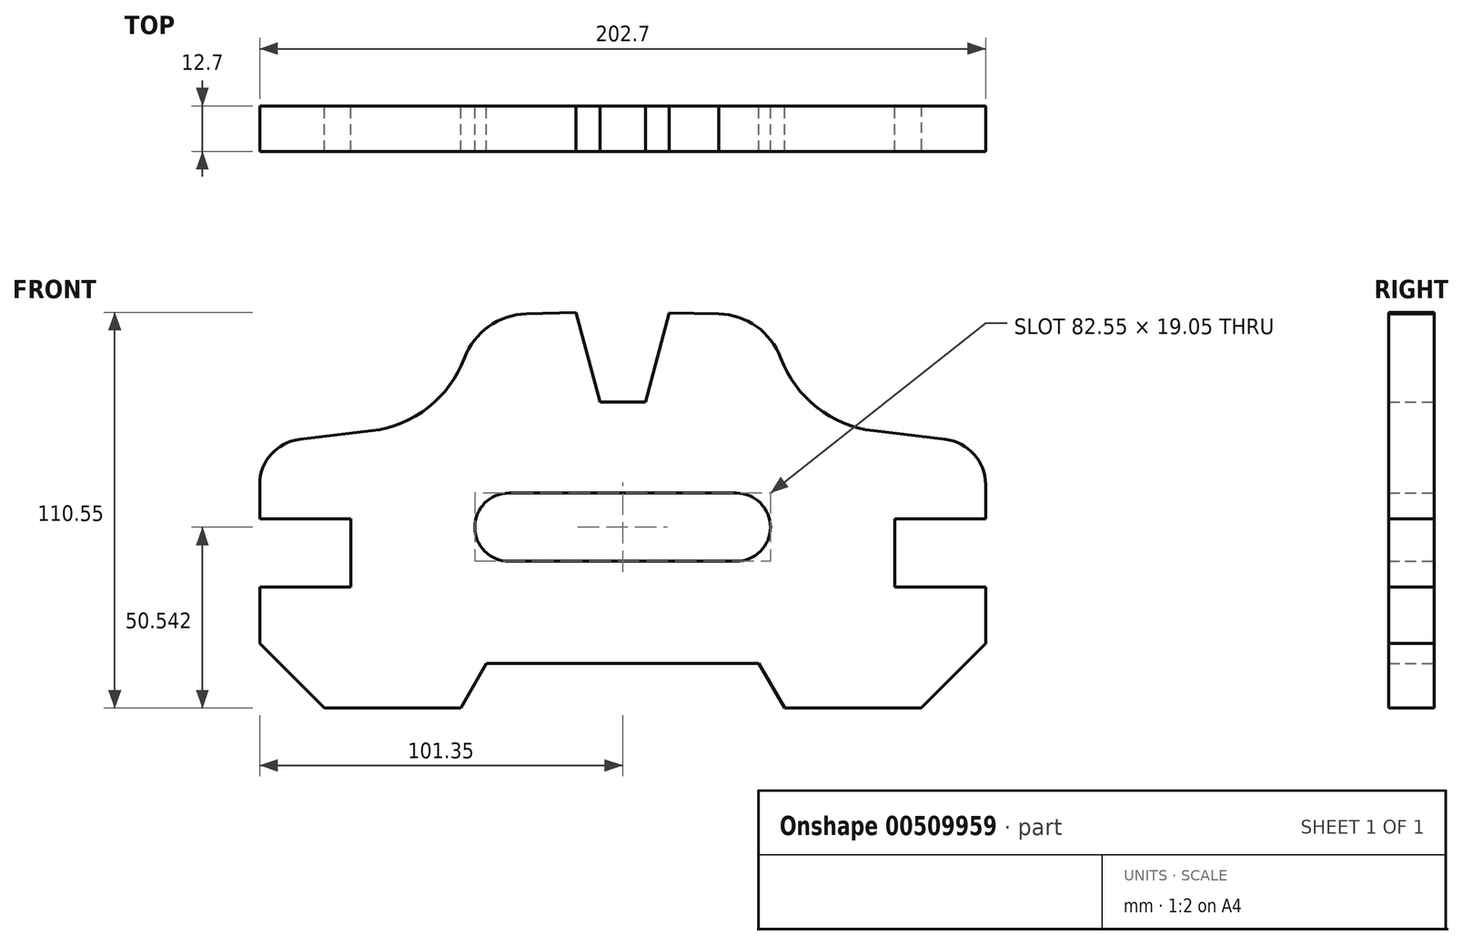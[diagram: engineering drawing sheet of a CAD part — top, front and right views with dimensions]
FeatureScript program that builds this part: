
annotation { "Feature Type Name" : "Feature", "Feature Type Description" : "" }
export const myFeature = defineFeature(function(context is Context, id is Id, definition is map)
    precondition{}
    {
        {
            var Q0;
            Q0=qCreatedBy(makeId("Front.planeOp"),FACE);
            var sketch = newSketch(context, id + "F0", { "sketchPlane" : qUnion([Q0])});
            skLineSegment(sketch, "E0", {"start": v(0, 64.43) * mm, "end": v(0, -63.1) * mm, "construction": true});
            skLineSegment(sketch, "E1", {"start": v(38.03, -38.44) * mm, "end": v(45.21, -50.88) * mm});
            skLineSegment(sketch, "E2", {"start": v(45.21, -50.88) * mm, "end": v(101.35, -50.88) * mm});
            skLineSegment(sketch, "E3", {"start": v(101.35, -50.88) * mm, "end": v(101.35, -17.1) * mm});
            skLineSegment(sketch, "E4", {"start": v(101.35, -17.1) * mm, "end": v(75.95, -17.1) * mm});
            skLineSegment(sketch, "E5", {"start": v(75.95, -17.1) * mm, "end": v(75.95, 1.95) * mm});
            skLineSegment(sketch, "E6", {"start": v(75.95, 1.95) * mm, "end": v(101.35, 1.95) * mm});
            skLineSegment(sketch, "E7", {"start": v(101.35, 1.95) * mm, "end": v(101.35, 11.6) * mm});
            skLineSegment(sketch, "E8", {"start": v(38.03, -38.44) * mm, "end": v(0, -38.44) * mm});
            skLineSegment(sketch, "E9", {"start": v(0, 9.19) * mm, "end": v(31.75, 9.19) * mm});
            skLineSegment(sketch, "E10", {"start": v(0, -9.86) * mm, "end": v(31.75, -9.86) * mm});
            skLineSegment(sketch, "E11.MirrorCS", {"start": v(-101.35, 1.95) * mm, "end": v(-101.35, 11.6) * mm});
            skLineSegment(sketch, "E12.MirrorCS", {"start": v(-75.95, 1.95) * mm, "end": v(-101.35, 1.95) * mm});
            skLineSegment(sketch, "E13.MirrorCS", {"start": v(-75.95, -17.1) * mm, "end": v(-75.95, 1.95) * mm});
            skLineSegment(sketch, "E14.MirrorCS", {"start": v(-101.35, -17.1) * mm, "end": v(-75.95, -17.1) * mm});
            skLineSegment(sketch, "E15.MirrorCS", {"start": v(-101.35, -50.88) * mm, "end": v(-101.35, -17.1) * mm});
            skLineSegment(sketch, "E16.MirrorCS", {"start": v(-45.21, -50.88) * mm, "end": v(-101.35, -50.88) * mm});
            skLineSegment(sketch, "E17.MirrorCS", {"start": v(-38.03, -38.44) * mm, "end": v(-45.21, -50.88) * mm});
            skLineSegment(sketch, "E18.MirrorCS", {"start": v(-38.03, -38.44) * mm, "end": v(0, -38.44) * mm});
            skLineSegment(sketch, "E19.MirrorCS", {"start": v(0, -9.86) * mm, "end": v(-31.75, -9.86) * mm});
            skLineSegment(sketch, "E20.MirrorCS", {"start": v(0, 9.19) * mm, "end": v(-31.75, 9.19) * mm});
            skArc(sketch, "E21", {"start": v(-31.75, 9.19) * mm, "mid": v(-41.27, -0.34) * mm, "end": v(-31.75, -9.86) * mm});
            skArc(sketch, "E22", {"start": v(31.75, -9.86) * mm, "mid": v(41.27, -0.34) * mm, "end": v(31.75, 9.19) * mm});
            skLineSegment(sketch, "E23", {"start": v(0, 34.64) * mm, "end": v(6.35, 34.64) * mm});
            skLineSegment(sketch, "E24.MirrorCS", {"start": v(0, 34.64) * mm, "end": v(-6.35, 34.64) * mm});
            skLineSegment(sketch, "E25", {"start": v(6.35, 34.64) * mm, "end": v(6.35, 73.1) * mm, "construction": true});
            skLineSegment(sketch, "E26", {"start": v(-6.35, 34.64) * mm, "end": v(-6.35, 69.53) * mm, "construction": true});
            skLineSegment(sketch, "E27", {"start": v(38.03, -38.44) * mm, "end": v(38.03, -60.96) * mm, "construction": true});
            skLineSegment(sketch, "E28.MirrorCS", {"start": v(13.01, 59.51) * mm, "end": v(6.35, 34.64) * mm});
            skLineSegment(sketch, "E29.MirrorCS", {"start": v(-13.06, 59.67) * mm, "end": v(-6.35, 34.64) * mm});
            skLineSegment(sketch, "E30", {"start": v(-26.86, 59.28) * mm, "end": v(-13.06, 59.67) * mm});
            skLineSegment(sketch, "E31", {"start": v(13.01, 59.51) * mm, "end": v(26.86, 59.28) * mm});
            skArc(sketch, "E32", {"start": v(-101.35, 11.6) * mm, "mid": v(-98.14, 20.03) * mm, "end": v(-90.15, 24.21) * mm});
            skLineSegment(sketch, "E33", {"start": v(-90.15, 24.21) * mm, "end": v(-70.1, 26.6) * mm});
            skArc(sketch, "E34", {"start": v(-70.1, 26.6) * mm, "mid": v(-54.28, 33.14) * mm, "end": v(-44.15, 46.95) * mm});
            skArc(sketch, "E35", {"start": v(-44.15, 46.95) * mm, "mid": v(-37.38, 55.75) * mm, "end": v(-26.86, 59.28) * mm});
            skArc(sketch, "E36.MirrorCS", {"start": v(101.35, 11.6) * mm, "mid": v(98.14, 20.03) * mm, "end": v(90.15, 24.21) * mm});
            skLineSegment(sketch, "E37.MirrorCS", {"start": v(90.15, 24.21) * mm, "end": v(70.1, 26.6) * mm});
            skArc(sketch, "E38.MirrorCS", {"start": v(70.1, 26.6) * mm, "mid": v(54.28, 33.14) * mm, "end": v(44.15, 46.95) * mm});
            skArc(sketch, "E39.MirrorCS", {"start": v(44.15, 46.95) * mm, "mid": v(37.38, 55.75) * mm, "end": v(26.86, 59.28) * mm});
            skSolve(sketch);
        }
        {
            var Q0;
            Q0=makeQuery(id+"F0.imprint","IMPRINT",FACE,{"disambiguationData":[TD([[makeQuery(id+"F0.imprint","IMPRINT",EDGE,{"derivedFrom":sQuery(id+"F0.wireOp",EDGE,"E1")}),1.0]])]});
            extrude(context, id + "F1", {"entities" : qUnion([Q0]), "depth" : 12.7 * mm});
        }
        {
            var Q0;
            Q0=makeQuery(id+"F1.opExtrude","SWEPT_EDGE",EDGE,{"disambiguationData":[OSD([sQuery(id+"F0.wireOp",EDGE,"E15.MirrorCS"),sQuery(id+"F0.wireOp",EDGE,"E16.MirrorCS")])]});
            var Q1;
            Q1=makeQuery(id+"F1.opExtrude","SWEPT_EDGE",EDGE,{"disambiguationData":[OSD([sQuery(id+"F0.wireOp",EDGE,"E2"),sQuery(id+"F0.wireOp",EDGE,"E3")])]});
            chamfer(context, id + "F2", {"entities" : qUnion([Q0, Q1]), "width" : 18.03 * mm, "tangentPropagation" : true});
        }
    });
